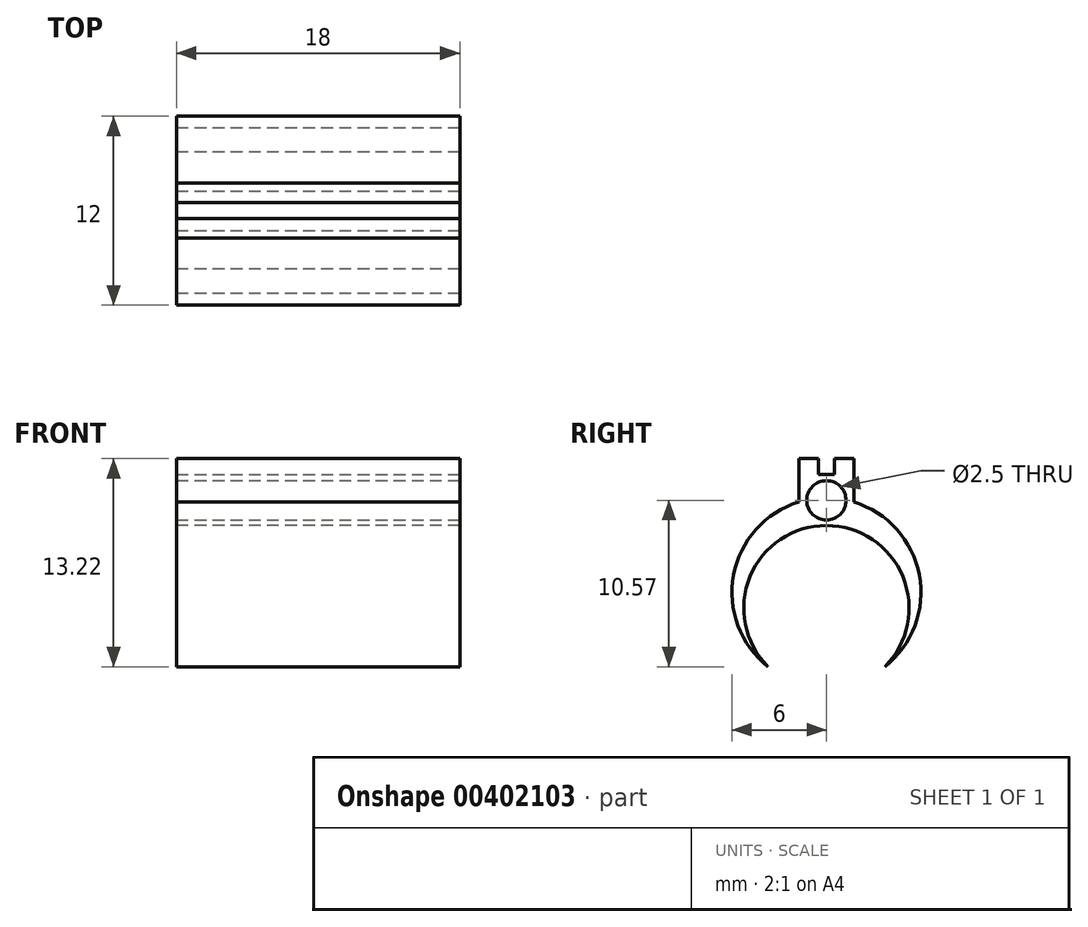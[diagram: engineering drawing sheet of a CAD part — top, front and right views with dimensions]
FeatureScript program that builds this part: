
annotation { "Feature Type Name" : "Feature", "Feature Type Description" : "" }
export const myFeature = defineFeature(function(context is Context, id is Id, definition is map)
    precondition{}
    {
        {
            var Q0;
            Q0=qCreatedBy(makeId("Top.planeOp"),FACE);
            var sketch = newSketch(context, id + "F0", { "sketchPlane" : qUnion([Q0])});
            skLineSegment(sketch, "E0.bottom", {"start": v(-9, 1.75) * mm, "end": v(9, 1.75) * mm});
            skLineSegment(sketch, "E0.top", {"start": v(-9, -1.75) * mm, "end": v(9, -1.75) * mm});
            skLineSegment(sketch, "E0.left", {"start": v(-9, 1.75) * mm, "end": v(-9, -1.75) * mm});
            skLineSegment(sketch, "E0.right", {"start": v(9, 1.75) * mm, "end": v(9, -1.75) * mm});
            skPoint(sketch, "E0.middle", {"position": v(0, 0) * mm});
            skSolve(sketch);
        }
        {
            var Q0;
            Q0 = qSketchRegion(id + "F0", true);
            extrude(context, id + "F1", {"entities" : qUnion([Q0]), "depth" : 2.5 * mm});
        }
        {
            var Q0;
            Q0=makeQuery(id+"F1.opExtrude","CAP_FACE",FACE,{"disambiguationData":[OSD([sQuery(id+"F0.wireOp",EDGE,"E0.bottom"),sQuery(id+"F0.wireOp",EDGE,"E0.top"),sQuery(id+"F0.wireOp",EDGE,"i61FBGkA-a5YL-a4x9-Gy4m-eUD6Uzz6ckKH"),sQuery(id+"F0.wireOp",EDGE,"HdGOV8dB-IFYb-9WW8-HcoN-fWssEOgspjJz")])],"isStart":false});
            var sketch = newSketch(context, id + "F2", { "sketchPlane" : qUnion([Q0])});
            skLineSegment(sketch, "E1.bottom", {"start": v(-9, 0.5) * mm, "end": v(9, 0.5) * mm});
            skLineSegment(sketch, "E1.top", {"start": v(-9, -0.5) * mm, "end": v(9, -0.5) * mm});
            skLineSegment(sketch, "E1.left", {"start": v(-9, 0.5) * mm, "end": v(-9, -0.5) * mm});
            skLineSegment(sketch, "E1.right", {"start": v(9, 0.5) * mm, "end": v(9, -0.5) * mm});
            skPoint(sketch, "E1.middle", {"position": v(0, 0) * mm});
            skCircle(sketch, "E2", {"center": v(9, 0) * mm, "radius": 0.5 * mm});
            skCircle(sketch, "E3", {"center": v(-9, 0) * mm, "radius": 0.5 * mm});
            skSolve(sketch);
        }
        {
            var Q0;
            Q0 = qSketchRegion(id + "F2", true);
            extrude(context, id + "F3", {"entities" : qUnion([Q0]), "operationType" : NewBodyOperationType.REMOVE, "oppositeDirection" : true, "depth" : 1 * mm});
        }
        {
            var Q0;
            Q0=makeQuery(id+"F1.opExtrude","CAP_FACE",FACE,{"disambiguationData":[OSD([sQuery(id+"F0.wireOp",EDGE,"E0.bottom"),sQuery(id+"F0.wireOp",EDGE,"E0.top"),sQuery(id+"F0.wireOp",EDGE,"i61FBGkA-a5YL-a4x9-Gy4m-eUD6Uzz6ckKH"),sQuery(id+"F0.wireOp",EDGE,"HdGOV8dB-IFYb-9WW8-HcoN-fWssEOgspjJz")])],"isStart":true});
            var sketch = newSketch(context, id + "F4", { "sketchPlane" : qUnion([Q0])});
            skLineSegment(sketch, "E4.bottom", {"start": v(-9, 1.75) * mm, "end": v(9, 1.75) * mm});
            skLineSegment(sketch, "E4.top", {"start": v(-9, -1.75) * mm, "end": v(9, -1.75) * mm});
            skLineSegment(sketch, "E4.left", {"start": v(-9, 1.75) * mm, "end": v(-9, -1.75) * mm});
            skLineSegment(sketch, "E4.right", {"start": v(9, 1.75) * mm, "end": v(9, -1.75) * mm});
            skSolve(sketch);
        }
        {
            var Q0;
            Q0 = qSketchRegion(id + "F4", true);
            extrude(context, id + "F5", {"entities" : qUnion([Q0]), "operationType" : NewBodyOperationType.ADD, "depth" : 0.5 * mm});
        }
        {
            var Q0;
            Q0=makeQuery(id+"F5.boolean.opBoolean","MERGE",FACE,{"derivedFrom":[makeQuery(id+"F1.opExtrude","SWEPT_FACE",FACE,{"disambiguationData":[OSD([sQuery(id+"F0.wireOp",EDGE,"E0.left")])]}),makeQuery(id+"F5.opExtrude","SWEPT_FACE",FACE,{"disambiguationData":[OSD([sQuery(id+"F4.wireOp",EDGE,"E4.left")])]})]});
            var sketch = newSketch(context, id + "F6", { "sketchPlane" : qUnion([Q0])});
            skCircle(sketch, "E5", {"center": v(0, -6) * mm, "radius": 6 * mm});
            skCircle(sketch, "E6", {"center": v(0, -7) * mm, "radius": 5.25 * mm});
            skSolve(sketch);
        }
        {
            var Q0;
            {var subQ4=sQuery(id+"F4.wireOp",EDGE,"E4.left");var subQ8=makeQuery(id+"F5.opExtrude","CAP_EDGE",EDGE,{"disambiguationData":[OSD([subQ4])],"isStart":false});Q0=makeQuery(id+"F6.imprint","IMPRINT",FACE,{"disambiguationData":[TD([[makeQuery(id+"F6.imprint","IMPRINT",EDGE,{"derivedFrom":subQ8}),-1.0]])]});}
            extrude(context, id + "F7", {"entities" : qUnion([Q0]), "operationType" : NewBodyOperationType.ADD, "oppositeDirection" : true, "depth" : 18 * mm});
        }
        {
            var Q0;
            Q0=makeQuery(id+"F7.boolean.opBoolean","MERGE",FACE,{"derivedFrom":[makeQuery(id+"F5.boolean.opBoolean","MERGE",FACE,{"derivedFrom":[makeQuery(id+"F1.opExtrude","SWEPT_FACE",FACE,{"disambiguationData":[OSD([sQuery(id+"F0.wireOp",EDGE,"E0.right")])]}),makeQuery(id+"F5.opExtrude","SWEPT_FACE",FACE,{"disambiguationData":[OSD([sQuery(id+"F4.wireOp",EDGE,"E4.right")])]})]}),makeQuery(id+"F7.opExtrude","CAP_FACE",FACE,{"disambiguationData":[OSD([sQuery(id+"F0.wireOp",EDGE,"E0.bottom"),sQuery(id+"F0.wireOp",EDGE,"E0.top"),sQuery(id+"F0.wireOp",EDGE,"E0.left"),sQuery(id+"F4.wireOp",EDGE,"E4.bottom"),sQuery(id+"F4.wireOp",EDGE,"E4.top"),sQuery(id+"F4.wireOp",EDGE,"E4.left"),sQuery(id+"F6.wireOp",EDGE,"E5"),sQuery(id+"F6.wireOp",EDGE,"E6")])],"isStart":false})]});
            var sketch = newSketch(context, id + "F8", { "sketchPlane" : qUnion([Q0])});
            skCircle(sketch, "E7", {"center": v(0, -0.15) * mm, "radius": 1.25 * mm});
            skSolve(sketch);
        }
        {
            var Q0;
            Q0=makeQuery(id+"F8.imprint","IMPRINT",FACE,{"disambiguationData":[TD([[makeQuery(id+"F8.imprint","IMPRINT",EDGE,{"derivedFrom":sQuery(id+"F8.wireOp",EDGE,"E7")}),1.0]])]});
            extrude(context, id + "F9", {"entities" : qUnion([Q0]), "operationType" : NewBodyOperationType.REMOVE, "endBound" : BoundingType.THROUGH_ALL, "oppositeDirection" : true, "depth" : 25 * mm});
        }
    });
